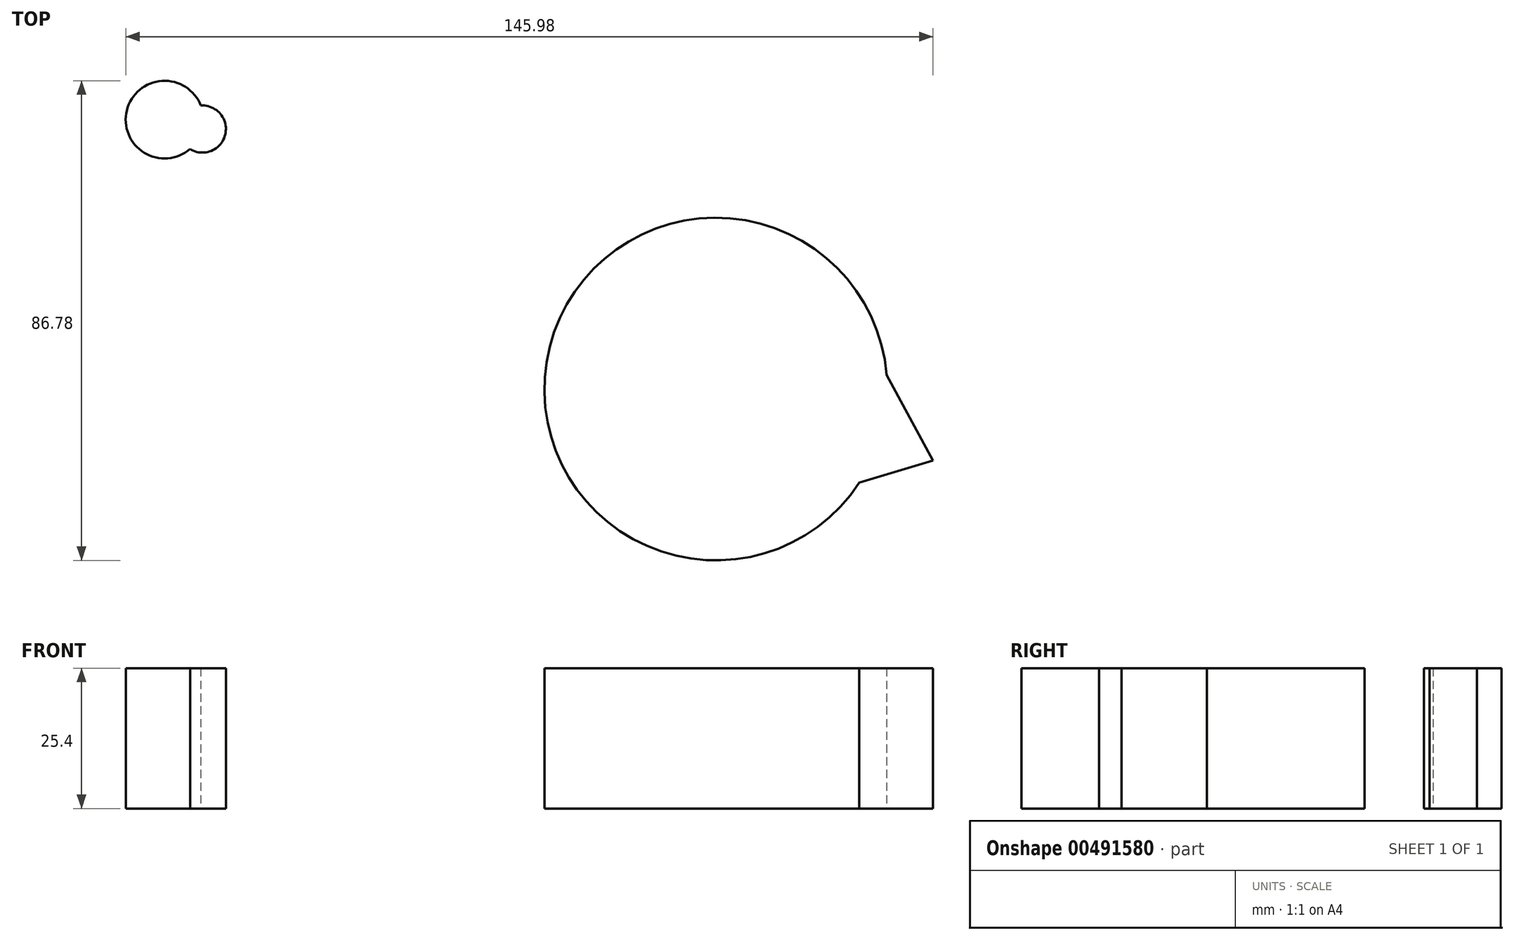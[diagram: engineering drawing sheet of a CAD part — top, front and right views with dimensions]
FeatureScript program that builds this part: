
annotation { "Feature Type Name" : "Feature", "Feature Type Description" : "" }
export const myFeature = defineFeature(function(context is Context, id is Id, definition is map)
    precondition{}
    {
        {
            var Q0;
            Q0=qCreatedBy(makeId("Top.planeOp"),FACE);
            var sketch = newSketch(context, id + "F0", { "sketchPlane" : qUnion([Q0])});
            skArc(sketch, "E0", {"start": v(30.9, 2.54) * mm, "mid": v(-30.05, 7.63) * mm, "end": v(25.95, -16.96) * mm});
            skLineSegment(sketch, "E1", {"start": v(30.9, 2.54) * mm, "end": v(39.28, -12.92) * mm});
            skLineSegment(sketch, "E2", {"start": v(39.28, -12.92) * mm, "end": v(25.95, -16.96) * mm});
            skSolve(sketch);
        }
        {
            var Q0;
            Q0 = qSketchRegion(id + "F0", true);
            extrude(context, id + "F1", {"entities" : qUnion([Q0]), "depth" : 25.4 * mm});
        }
        {
            var Q0;
            Q0=qCreatedBy(makeId("Top.planeOp"),FACE);
            var sketch = newSketch(context, id + "F2", { "sketchPlane" : qUnion([Q0])});
            skCircle(sketch, "E3", {"center": v(-99.67, 48.75) * mm, "radius": 7.03 * mm});
            skCircle(sketch, "E4", {"center": v(-92.85, 47.05) * mm, "radius": 4.26 * mm});
            skSolve(sketch);
        }
        {
            var Q0;
            Q0 = qSketchRegion(id + "F2", true);
            extrude(context, id + "F3", {"entities" : qUnion([Q0]), "depth" : 25.4 * mm});
        }
    });
